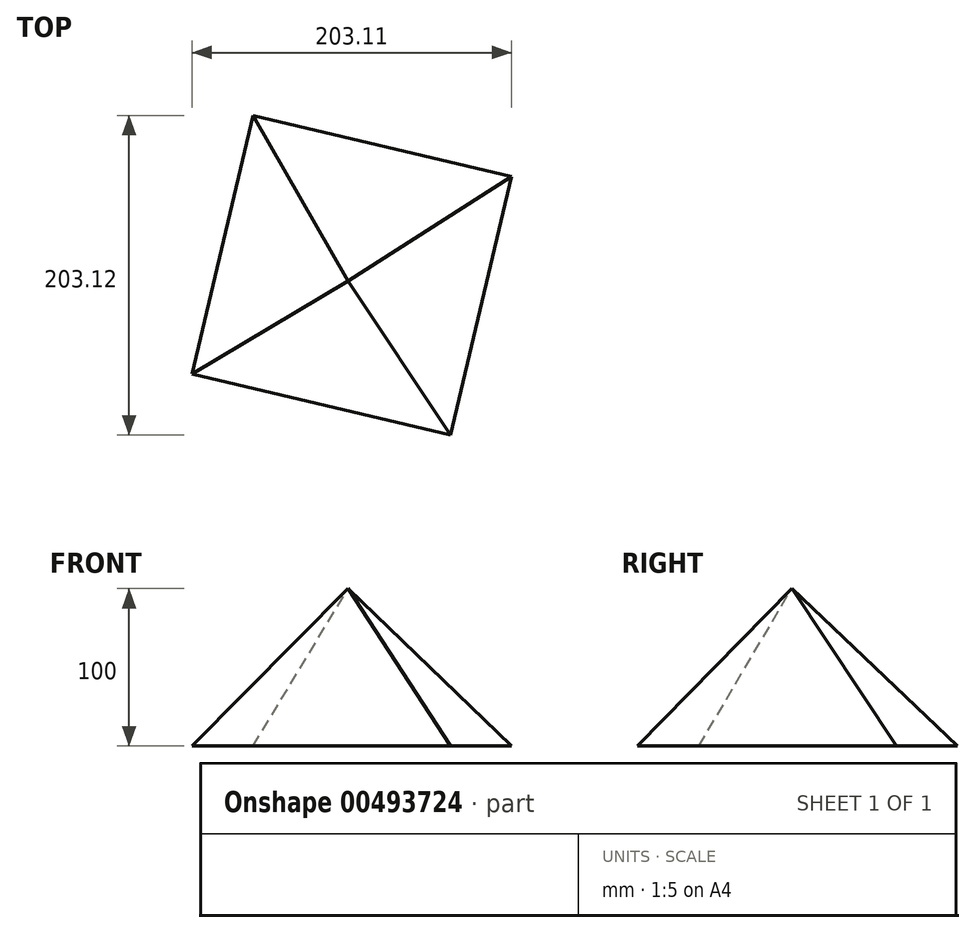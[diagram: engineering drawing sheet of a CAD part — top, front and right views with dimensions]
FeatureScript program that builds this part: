
annotation { "Feature Type Name" : "Feature", "Feature Type Description" : "" }
export const myFeature = defineFeature(function(context is Context, id is Id, definition is map)
    precondition{}
    {
        {
            var Q0;
            Q0=qCreatedBy(makeId("Top.planeOp"),FACE);
            var sketch = newSketch(context, id + "F0", { "sketchPlane" : qUnion([Q0])});
            skCircle(sketch, "E0.cCircle", {"center": v(2.3, 0) * mm, "radius": 119.35 * mm, "construction": true});
            skLineSegment(sketch, "E0.0", {"start": v(103.85, 62.68) * mm, "end": v(64.98, -101.56) * mm});
            skLineSegment(sketch, "E0.1", {"start": v(64.98, -101.56) * mm, "end": v(-99.26, -62.68) * mm});
            skLineSegment(sketch, "E0.2", {"start": v(-99.26, -62.68) * mm, "end": v(-60.39, 101.56) * mm});
            skLineSegment(sketch, "E0.3", {"start": v(-60.39, 101.56) * mm, "end": v(103.85, 62.68) * mm});
            skSolve(sketch);
        }
        {
            var Q0;
            Q0=qCreatedBy(makeId("Top.planeOp"),FACE);
            cPlane(context, id + "F1", {"entities" : qUnion([Q0]), "cplaneType" : CPlaneType.OFFSET, "offset" : 100 * mm, "width" : 150 * mm, "height" : 150 * mm});
        }
        {
            var Q0;
            Q0=qCreatedBy(id+"F1.planeOp",FACE);
            var sketch = newSketch(context, id + "F2", { "sketchPlane" : qUnion([Q0])});
            skPoint(sketch, "E1", {"position": v(0, -3.72) * mm});
            skSolve(sketch);
        }
        {
            var Q0;
            Q0=makeQuery(id+"F0.imprint","IMPRINT",FACE,{"disambiguationData":[TD([[makeQuery(id+"F0.imprint","IMPRINT",EDGE,{"derivedFrom":sQuery(id+"F0.wireOp",EDGE,"E0.0")}),-1.0]])]});
            var Q1;
            Q1=sQuery(id+"F2.wireOp",VERTEX,"E1");
            loft(context, id + "F3", {"sheetProfilesArray" : [{ "sheetProfileEntities" : qUnion([Q0]) }, { "sheetProfileEntities" : qUnion([Q1]) }]});
        }
    });
